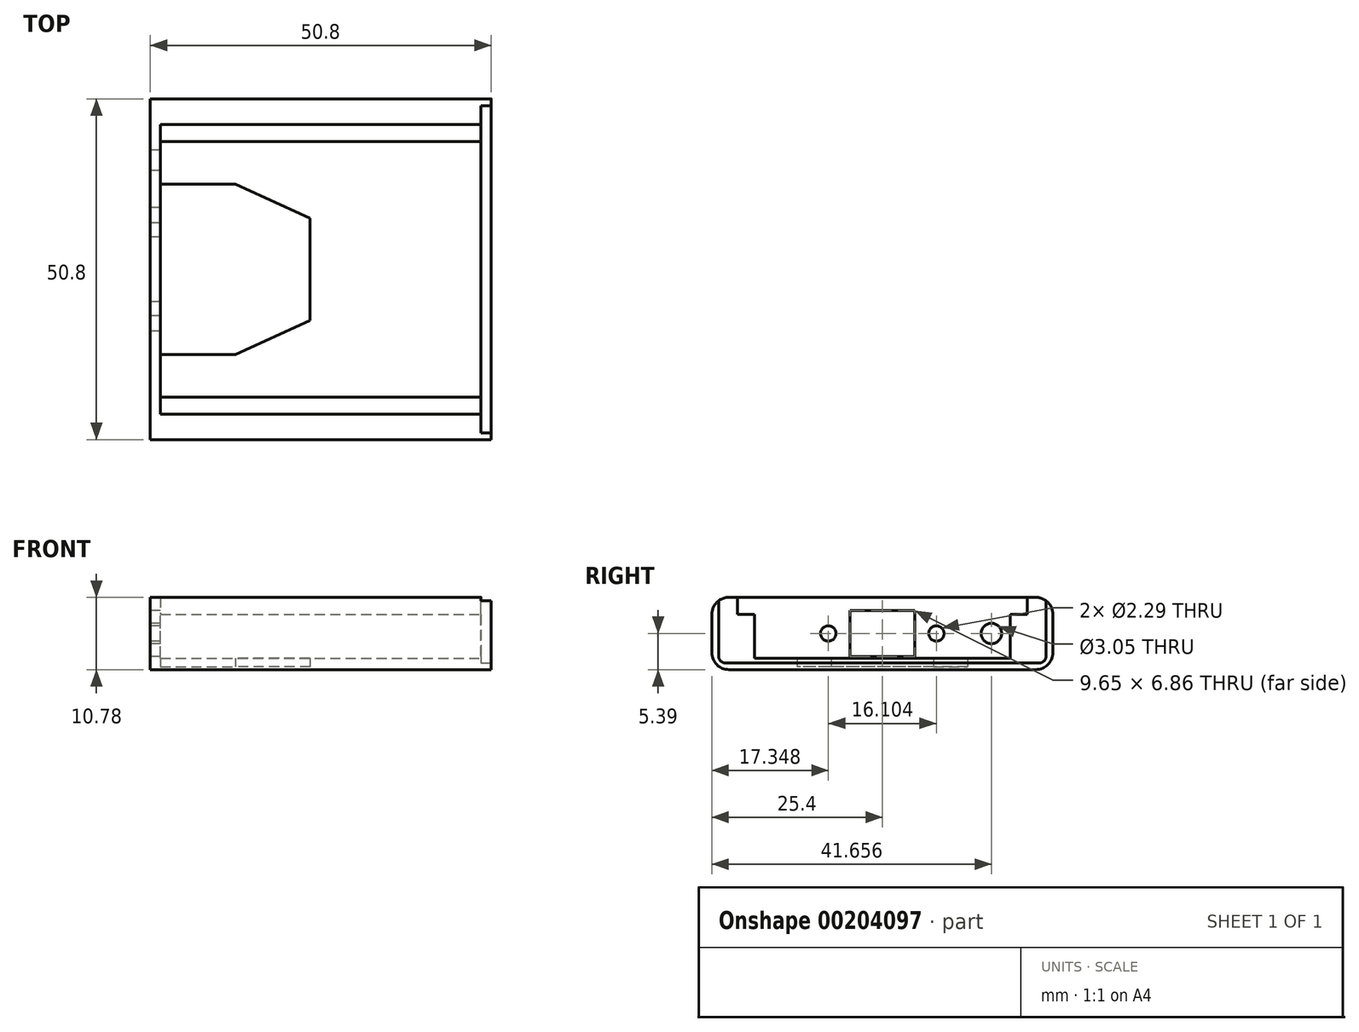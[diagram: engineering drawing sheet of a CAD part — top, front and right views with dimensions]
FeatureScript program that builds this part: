
annotation { "Feature Type Name" : "Feature", "Feature Type Description" : "" }
export const myFeature = defineFeature(function(context is Context, id is Id, definition is map)
    precondition{}
    {
        {
            var Q0;
            Q0=qCreatedBy(makeId("Top.planeOp"),FACE);
            var sketch = newSketch(context, id + "F0", { "sketchPlane" : qUnion([Q0])});
            skLineSegment(sketch, "E0.bottom", {"start": v(-25.4, 25.4) * mm, "end": v(25.4, 25.4) * mm});
            skLineSegment(sketch, "E0.top", {"start": v(-25.4, -25.4) * mm, "end": v(25.4, -25.4) * mm});
            skLineSegment(sketch, "E0.left", {"start": v(-25.4, 25.4) * mm, "end": v(-25.4, -25.4) * mm});
            skLineSegment(sketch, "E0.right", {"start": v(25.4, 25.4) * mm, "end": v(25.4, -25.4) * mm});
            skPoint(sketch, "E0.middle", {"position": v(0, 0) * mm});
            skSolve(sketch);
        }
        {
            var Q0;
            Q0 = qSketchRegion(id + "F0", true);
            extrude(context, id + "F1", {"entities" : qUnion([Q0]), "depth" : 10.78 * mm});
        }
        {
            var Q0;
            Q0=makeQuery(id+"F1.opExtrude","CAP_EDGE",EDGE,{"disambiguationData":[OSD([sQuery(id+"F0.wireOp",EDGE,"E0.bottom")])],"isStart":false});
            var Q1;
            Q1=makeQuery(id+"F1.opExtrude","CAP_EDGE",EDGE,{"disambiguationData":[OSD([sQuery(id+"F0.wireOp",EDGE,"E0.top")])],"isStart":false});
            var Q2;
            Q2=makeQuery(id+"F1.opExtrude","CAP_EDGE",EDGE,{"disambiguationData":[OSD([sQuery(id+"F0.wireOp",EDGE,"E0.top")])],"isStart":true});
            var Q3;
            Q3=makeQuery(id+"F1.opExtrude","CAP_EDGE",EDGE,{"disambiguationData":[OSD([sQuery(id+"F0.wireOp",EDGE,"E0.bottom")])],"isStart":true});
            fillet(context, id + "F2", {"entities" : qUnion([Q0, Q1, Q2, Q3]), "radius" : 2.54 * mm, "tangentPropagation" : true, "allowEdgeOverflow" : false});
        }
        {
            var Q0;
            Q0=makeQuery(id+"F1.opExtrude","SWEPT_FACE",FACE,{"disambiguationData":[OSD([sQuery(id+"F0.wireOp",EDGE,"E0.right")])]});
            var sketch = newSketch(context, id + "F3", { "sketchPlane" : qUnion([Q0])});
            skLineSegment(sketch, "E1.bottom", {"start": v(19.05, 0.4) * mm, "end": v(-19.05, 0.4) * mm});
            skLineSegment(sketch, "E1.top", {"start": v(19.05, 13.1) * mm, "end": v(-19.05, 13.1) * mm});
            skLineSegment(sketch, "E1.left", {"start": v(19.05, 0.4) * mm, "end": v(19.05, 13.1) * mm});
            skLineSegment(sketch, "E1.right", {"start": v(-19.05, 0.4) * mm, "end": v(-19.05, 13.1) * mm});
            skPoint(sketch, "E1.middle", {"position": v(0, 6.75) * mm});
            skSolve(sketch);
        }
        {
            var Q0;
            Q0 = qSketchRegion(id + "F3", true);
            extrude(context, id + "F4", {"entities" : qUnion([Q0]), "operationType" : NewBodyOperationType.REMOVE, "oppositeDirection" : true, "depth" : 49.28 * mm});
        }
        {
            var Q0;
            Q0=makeQuery(id+"F1.opExtrude","SWEPT_FACE",FACE,{"disambiguationData":[OSD([sQuery(id+"F0.wireOp",EDGE,"E0.left")])]});
            var sketch = newSketch(context, id + "F5", { "sketchPlane" : qUnion([Q0])});
            skLineSegment(sketch, "E2.bottom", {"start": v(-4.83, 8.82) * mm, "end": v(4.83, 8.82) * mm});
            skLineSegment(sketch, "E2.top", {"start": v(-4.83, 1.96) * mm, "end": v(4.83, 1.96) * mm});
            skLineSegment(sketch, "E2.left", {"start": v(-4.83, 8.82) * mm, "end": v(-4.83, 1.96) * mm});
            skLineSegment(sketch, "E2.right", {"start": v(4.83, 8.82) * mm, "end": v(4.83, 1.96) * mm});
            skPoint(sketch, "E2.middle", {"position": v(0, 5.39) * mm});
            skLineSegment(sketch, "E3", {"start": v(0, 0) * mm, "end": v(0, 10.78) * mm, "construction": true});
            skCircle(sketch, "E4", {"center": v(-16.26, 5.39) * mm, "radius": 1.52 * mm});
            skCircle(sketch, "E5", {"center": v(-8.05, 5.39) * mm, "radius": 1.14 * mm});
            skCircle(sketch, "E6", {"center": v(8.05, 5.39) * mm, "radius": 1.14 * mm});
            skSolve(sketch);
        }
        {
            var Q0;
            Q0 = qSketchRegion(id + "F5", true);
            extrude(context, id + "F6", {"entities" : qUnion([Q0]), "operationType" : NewBodyOperationType.REMOVE, "oppositeDirection" : true, "depth" : 1.78 * mm});
        }
        {
            var Q0;
            Q0=makeQuery(id+"F4.boolean.opBoolean","COPY",FACE,{"derivedFrom":makeQuery(id+"F4.opExtrude","SWEPT_FACE",FACE,{"disambiguationData":[OSD([sQuery(id+"F3.wireOp",EDGE,"E1.bottom")])]})});
            var sketch = newSketch(context, id + "F7", { "sketchPlane" : qUnion([Q0])});
            skLineSegment(sketch, "E7.bottom", {"start": v(-1.59, 19.05) * mm, "end": v(1.59, 19.05) * mm});
            skLineSegment(sketch, "E7.top", {"start": v(-1.59, -19.05) * mm, "end": v(1.59, -19.05) * mm});
            skLineSegment(sketch, "E7.left", {"start": v(-1.59, 7.62) * mm, "end": v(-1.59, -7.62) * mm});
            skLineSegment(sketch, "E8", {"start": v(0, 19.05) * mm, "end": v(0, -19.05) * mm, "construction": true});
            skLineSegment(sketch, "E9.bottom", {"start": v(7.94, 19.05) * mm, "end": v(11.11, 19.05) * mm});
            skLineSegment(sketch, "E9.top", {"start": v(7.94, -19.05) * mm, "end": v(11.11, -19.05) * mm});
            skLineSegment(sketch, "E10.bottom", {"start": v(-23.88, 12.7) * mm, "end": v(-12.73, 12.7) * mm});
            skLineSegment(sketch, "E10.left", {"start": v(-23.88, 12.7) * mm, "end": v(-23.88, 15.88) * mm});
            skLineSegment(sketch, "E11.bottom", {"start": v(-23.88, -12.7) * mm, "end": v(-12.73, -12.7) * mm});
            skLineSegment(sketch, "E11.left", {"start": v(-23.88, -12.7) * mm, "end": v(-23.88, -15.88) * mm});
            skLineSegment(sketch, "E12.bottom", {"start": v(11.11, -12.7) * mm, "end": v(25.4, -12.7) * mm});
            skLineSegment(sketch, "E13", {"start": v(-23.88, 0) * mm, "end": v(25.4, 0) * mm, "construction": true});
            skLineSegment(sketch, "E14", {"start": v(1.59, 0) * mm, "end": v(7.94, 0) * mm, "construction": true});
            skLineSegment(sketch, "E15", {"start": v(-1.59, 7.62) * mm, "end": v(-12.73, 12.7) * mm});
            skLineSegment(sketch, "E16", {"start": v(-1.59, -7.62) * mm, "end": v(-12.73, -12.7) * mm});
            skPoint(sketch, "E17.trimOffspring.start.orphan", {"position": v(-1.59, -12.7) * mm});
            skPoint(sketch, "E18.trimOffspring.end.orphan", {"position": v(1.59, -6.35) * mm});
            skPoint(sketch, "E19.orphan", {"position": v(7.94, -6.35) * mm});
            skPoint(sketch, "E20.orphan", {"position": v(7.94, 6.35) * mm});
            skPoint(sketch, "E7.right.end.orphan", {"position": v(1.59, 6.35) * mm});
            skPoint(sketch, "E21.orphan", {"position": v(-7.16, 12.7) * mm});
            skPoint(sketch, "E22.orphan", {"position": v(-1.59, 10.16) * mm});
            skPoint(sketch, "E23.orphan", {"position": v(-7.16, -12.7) * mm});
            skPoint(sketch, "E24.orphan", {"position": v(-1.59, -10.16) * mm});
            skLineSegment(sketch, "E25", {"start": v(-23.88, 12.7) * mm, "end": v(-23.88, 19.05) * mm});
            skLineSegment(sketch, "E26", {"start": v(-23.88, 19.05) * mm, "end": v(25.4, 19.05) * mm});
            skLineSegment(sketch, "E27", {"start": v(25.4, 19.05) * mm, "end": v(25.4, -19.05) * mm});
            skLineSegment(sketch, "E28", {"start": v(25.4, -19.05) * mm, "end": v(-23.88, -19.05) * mm});
            skLineSegment(sketch, "E29", {"start": v(-23.88, -19.05) * mm, "end": v(-23.88, -12.7) * mm});
            skSolve(sketch);
        }
        {
            var Q0;
            Q0 = qSketchRegion(id + "F7", true);
            extrude(context, id + "F8", {"entities" : qUnion([Q0]), "operationType" : NewBodyOperationType.ADD, "depth" : 1.27 * mm});
        }
        {
            var Q0;
            Q0=makeQuery(id+"F8.boolean.opBoolean","MERGE",FACE,{"derivedFrom":[makeQuery(id+"F1.opExtrude","SWEPT_FACE",FACE,{"disambiguationData":[OSD([sQuery(id+"F0.wireOp",EDGE,"E0.right")])]}),makeQuery(id+"F8.opExtrude","SWEPT_FACE",FACE,{"disambiguationData":[OSD([sQuery(id+"F7.wireOp",EDGE,"1NSGLjiZ-oQ3a-62qk-CTgt-9jtmtN1lsz67.right")])]}),makeQuery(id+"F8.opExtrude","SWEPT_FACE",FACE,{"disambiguationData":[OSD([sQuery(id+"F7.wireOp",EDGE,"E12.right")])]})]});
            var sketch = newSketch(context, id + "F9", { "sketchPlane" : qUnion([Q0])});
            skLineSegment(sketch, "E30.bottom", {"start": v(-21.59, 10.78) * mm, "end": v(21.59, 10.78) * mm});
            skLineSegment(sketch, "E30.top", {"start": v(-21.59, 8.24) * mm, "end": v(21.59, 8.24) * mm});
            skLineSegment(sketch, "E30.left", {"start": v(-21.59, 10.78) * mm, "end": v(-21.59, 8.24) * mm});
            skLineSegment(sketch, "E30.right", {"start": v(21.59, 10.78) * mm, "end": v(21.59, 8.24) * mm});
            skSolve(sketch);
        }
        {
            var Q0;
            Q0 = qSketchRegion(id + "F9", true);
            extrude(context, id + "F10", {"entities" : qUnion([Q0]), "operationType" : NewBodyOperationType.REMOVE, "oppositeDirection" : true, "depth" : 49.28 * mm});
        }
        {
            var Q0;
            Q0=makeQuery(id+"F8.boolean.opBoolean","MERGE",FACE,{"derivedFrom":[makeQuery(id+"F1.opExtrude","SWEPT_FACE",FACE,{"disambiguationData":[OSD([sQuery(id+"F0.wireOp",EDGE,"E0.right")])]}),makeQuery(id+"F8.opExtrude","SWEPT_FACE",FACE,{"disambiguationData":[OSD([sQuery(id+"F7.wireOp",EDGE,"1NSGLjiZ-oQ3a-62qk-CTgt-9jtmtN1lsz67.right")])]}),makeQuery(id+"F8.opExtrude","SWEPT_FACE",FACE,{"disambiguationData":[OSD([sQuery(id+"F7.wireOp",EDGE,"E12.right")])]})]});
            var sketch = newSketch(context, id + "F11", { "sketchPlane" : qUnion([Q0])});
            skLineSegment(sketch, "E31.bottom", {"start": v(-23.4, 1) * mm, "end": v(23.4, 1) * mm});
            skLineSegment(sketch, "E31.top", {"start": v(-23.4, 9.78) * mm, "end": v(23.4, 9.78) * mm});
            skLineSegment(sketch, "E31.left", {"start": v(-24.4, 2) * mm, "end": v(-24.4, 8.78) * mm});
            skLineSegment(sketch, "E31.right", {"start": v(24.4, 2) * mm, "end": v(24.4, 8.78) * mm});
            skPoint(sketch, "E32.visualSharp", {"position": v(-24.4, 9.78) * mm});
            skArc(sketch, "E32.filletArc", {"start": v(-23.4, 9.78) * mm, "mid": v(-24.1, 9.49) * mm, "end": v(-24.4, 8.78) * mm});
            skPoint(sketch, "E33.visualSharp", {"position": v(-24.4, 1) * mm});
            skArc(sketch, "E33.filletArc", {"start": v(-24.4, 2) * mm, "mid": v(-24.1, 1.3) * mm, "end": v(-23.4, 1) * mm});
            skPoint(sketch, "E34.visualSharp", {"position": v(24.4, 1) * mm});
            skArc(sketch, "E34.filletArc", {"start": v(23.4, 1) * mm, "mid": v(24.1, 1.3) * mm, "end": v(24.4, 2) * mm});
            skPoint(sketch, "E35.visualSharp", {"position": v(24.4, 9.78) * mm});
            skArc(sketch, "E35.filletArc", {"start": v(24.4, 8.78) * mm, "mid": v(24.1, 9.49) * mm, "end": v(23.4, 9.78) * mm});
            skSolve(sketch);
        }
        {
            var Q0;
            Q0 = qSketchRegion(id + "F11", true);
            extrude(context, id + "F12", {"entities" : qUnion([Q0]), "operationType" : NewBodyOperationType.REMOVE, "oppositeDirection" : true, "depth" : 1.5 * mm});
        }
        {
            var Q0;
            Q0=makeQuery(id+"F8.boolean.opBoolean","MERGE",FACE,{"derivedFrom":[makeQuery(id+"F1.opExtrude","SWEPT_FACE",FACE,{"disambiguationData":[OSD([sQuery(id+"F0.wireOp",EDGE,"E0.right")])]}),makeQuery(id+"F8.opExtrude","SWEPT_FACE",FACE,{"disambiguationData":[OSD([sQuery(id+"F7.wireOp",EDGE,"E27")])]})]});
            var sketch = newSketch(context, id + "F13", { "sketchPlane" : qUnion([Q0])});
            skLineSegment(sketch, "E36", {"start": v(25.4, 8.24) * mm, "end": v(24.4, 8.24) * mm, "construction": true});
            skLineSegment(sketch, "E37.bottom", {"start": v(24.4, 8.24) * mm, "end": v(21.59, 8.24) * mm});
            skLineSegment(sketch, "E37.top", {"start": v(24.4, 10.78) * mm, "end": v(21.59, 10.78) * mm});
            skLineSegment(sketch, "E37.left", {"start": v(24.4, 8.24) * mm, "end": v(24.4, 10.78) * mm});
            skLineSegment(sketch, "E37.right", {"start": v(21.59, 8.24) * mm, "end": v(21.59, 10.78) * mm});
            skSolve(sketch);
        }
        {
            var Q0;
            Q0 = qSketchRegion(id + "F13", true);
            extrude(context, id + "F14", {"entities" : qUnion([Q0]), "operationType" : NewBodyOperationType.REMOVE, "oppositeDirection" : true, "depth" : 1.5 * mm});
        }
        {
            var Q0;
            Q0=makeQuery(id+"F8.boolean.opBoolean","MERGE",FACE,{"derivedFrom":[makeQuery(id+"F1.opExtrude","SWEPT_FACE",FACE,{"disambiguationData":[OSD([sQuery(id+"F0.wireOp",EDGE,"E0.right")])]}),makeQuery(id+"F8.opExtrude","SWEPT_FACE",FACE,{"disambiguationData":[OSD([sQuery(id+"F7.wireOp",EDGE,"E27")])]})]});
            var sketch = newSketch(context, id + "F15", { "sketchPlane" : qUnion([Q0])});
            skLineSegment(sketch, "E38", {"start": v(-25.4, 8.24) * mm, "end": v(-24.4, 8.24) * mm, "construction": true});
            skLineSegment(sketch, "E39.bottom", {"start": v(-24.4, 8.24) * mm, "end": v(-21.59, 8.24) * mm});
            skLineSegment(sketch, "E39.top", {"start": v(-24.4, 10.78) * mm, "end": v(-21.59, 10.78) * mm});
            skLineSegment(sketch, "E39.left", {"start": v(-24.4, 8.24) * mm, "end": v(-24.4, 10.78) * mm});
            skLineSegment(sketch, "E39.right", {"start": v(-21.59, 8.24) * mm, "end": v(-21.59, 10.78) * mm});
            skSolve(sketch);
        }
        {
            var Q0;
            Q0 = qSketchRegion(id + "F15", true);
            extrude(context, id + "F16", {"entities" : qUnion([Q0]), "operationType" : NewBodyOperationType.REMOVE, "oppositeDirection" : true, "depth" : 1.5 * mm});
        }
    });
